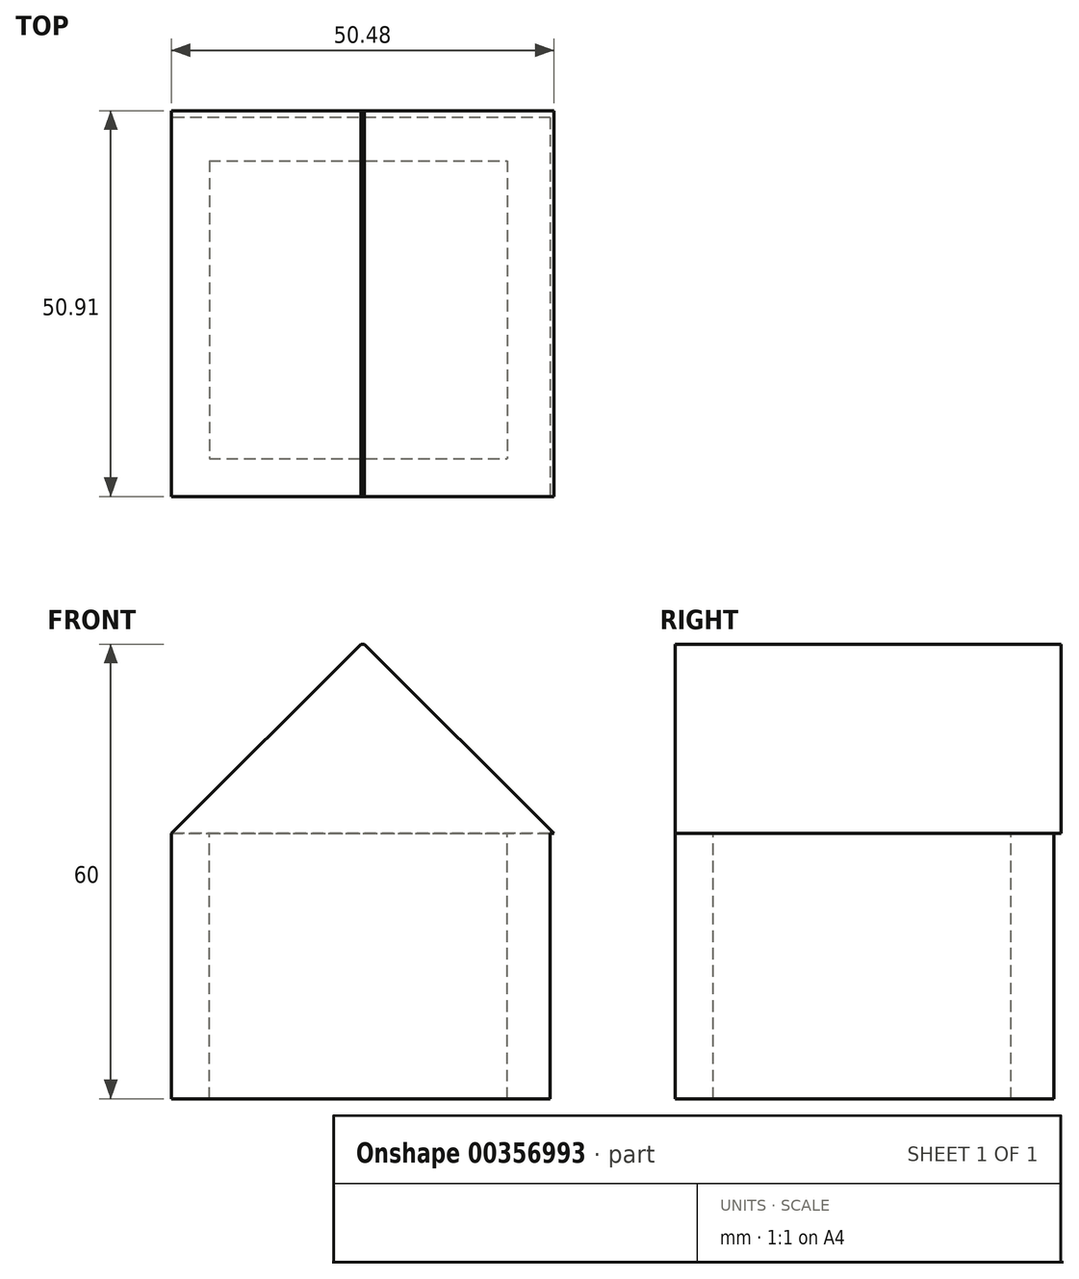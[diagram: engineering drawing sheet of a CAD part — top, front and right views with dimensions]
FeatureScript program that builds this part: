
annotation { "Feature Type Name" : "Feature", "Feature Type Description" : "" }
export const myFeature = defineFeature(function(context is Context, id is Id, definition is map)
    precondition{}
    {
        {
            var Q0;
            Q0=qCreatedBy(makeId("Top.planeOp"),FACE);
            var sketch = newSketch(context, id + "F0", { "sketchPlane" : qUnion([Q0])});
            skLineSegment(sketch, "E0.bottom", {"start": v(50, 50) * mm, "end": v(0, 50) * mm});
            skLineSegment(sketch, "E0.top", {"start": v(50, 0) * mm, "end": v(0, 0) * mm});
            skLineSegment(sketch, "E0.left", {"start": v(50, 50) * mm, "end": v(50, 0) * mm});
            skLineSegment(sketch, "E0.right", {"start": v(0, 50) * mm, "end": v(0, 0) * mm});
            skLineSegment(sketch, "E1.bottom", {"start": v(5, 5) * mm, "end": v(44.33, 5) * mm});
            skLineSegment(sketch, "E1.top", {"start": v(5, 44.33) * mm, "end": v(44.33, 44.33) * mm});
            skLineSegment(sketch, "E1.left", {"start": v(44.33, 44.33) * mm, "end": v(44.33, 5) * mm});
            skLineSegment(sketch, "E1.right", {"start": v(5, 44.33) * mm, "end": v(5, 5) * mm});
            skPoint(sketch, "E1.middle", {"position": v(24.67, 24.67) * mm});
            skLineSegment(sketch, "E2", {"start": v(24.67, 24.67) * mm, "end": v(24.67, 24.67) * mm});
            skSolve(sketch);
        }
        {
            var Q0;
            Q0=qCreatedBy(makeId("Top.planeOp"),FACE);
            var sketch = newSketch(context, id + "F1", { "sketchPlane" : qUnion([Q0])});
            skLineSegment(sketch, "E3.bottom", {"start": v(0, 50.91) * mm, "end": v(50.48, 50.91) * mm});
            skLineSegment(sketch, "E3.top", {"start": v(0, 0) * mm, "end": v(50.48, 0) * mm});
            skLineSegment(sketch, "E3.left", {"start": v(0, 50.91) * mm, "end": v(0, 0) * mm});
            skLineSegment(sketch, "E3.right", {"start": v(50.48, 50.91) * mm, "end": v(50.48, 0) * mm});
            skSolve(sketch);
        }
        {
            var Q0;
            Q0 = qSketchRegion(id + "F1", true);
            extrude(context, id + "F2", {"entities" : qUnion([Q0]), "depth" : 25 * mm});
        }
        {
            var Q0;
            Q0=makeQuery(id+"F0.imprint","IMPRINT",FACE,{"disambiguationData":[TD([[makeQuery(id+"F0.imprint","IMPRINT",EDGE,{"derivedFrom":sQuery(id+"F0.wireOp",EDGE,"E0.bottom")}),1.0]])]});
            extrude(context, id + "F3", {"entities" : qUnion([Q0]), "operationType" : NewBodyOperationType.ADD, "oppositeDirection" : true, "depth" : 35 * mm});
        }
        {
            var Q0;
            Q0=makeQuery(id+"F2.opExtrude","CAP_EDGE",EDGE,{"disambiguationData":[OSD([sQuery(id+"F1.wireOp",EDGE,"E3.right")])],"isStart":false});
            var Q1;
            Q1=makeQuery(id+"F2.opExtrude","CAP_EDGE",EDGE,{"disambiguationData":[OSD([sQuery(id+"F1.wireOp",EDGE,"E3.left")])],"isStart":false});
            chamfer(context, id + "F4", {"entities" : qUnion([Q0, Q1]), "chamferType" : ChamferType.OFFSET_ANGLE, "width" : 25 * mm, "oppositeDirection" : false, "angle" : 45 * degree, "tangentPropagation" : true});
        }
    });
